# Revit family: ASSA_ABLOY_CurvedCD_nonHosted
name_source: partatom
category: Doors
units: mm (PartAtom-declared; Revit-internal decimal feet)

## family parameters
Always vertical = Yes
Cut with Voids When Loaded = No
Room Calculation Point = No
Shared = No
Work Plane-Based = No

## types (1)
- Curved non hosted
    Analytic Construction = <None>
    BreakoutFacility = No
    Colour = Customer specific
    Default Elevation = 0 mm  [stored 0 ft]
    Define Thermal Properties by = Schematic Type
    DrumWallOptions = Glass, Sandwich panel
    FireExit = No
    FrameSeal = Yes
    GlassLayers = 0
    GlassThickness1 = 0 mm  [stored 0 ft]
    GlassThickness2 = 0 mm  [stored 0 ft]
    HandicapAccessible = Yes
    HasDrive = Yes
    IsExternal = Yes
    ManufacturerURL = www.record.group
    Material = Aluminium
    ModelReference = Depends on the configuration
    NominalHeight = 0 mm  [stored 0 ft]
    NominalLength = 0 mm  [stored 0 ft]
    NominalWidth = 0 mm  [stored 0 ft]
    ReplacementCost = Depends on the configuration and door type
    SelfClosing = Yes
    Shape = Rectangular shaped
    WarrantyDescription = Depends on country
    Weight = Depends on configuration and size

note: [stored X ft] marks values corroborated as IEEE doubles in the binary element streams (Revit-internal decimal feet)

## geometry (parser evidence)
native form markers: Sweep x19
no freeform markers — native parametric forms only
